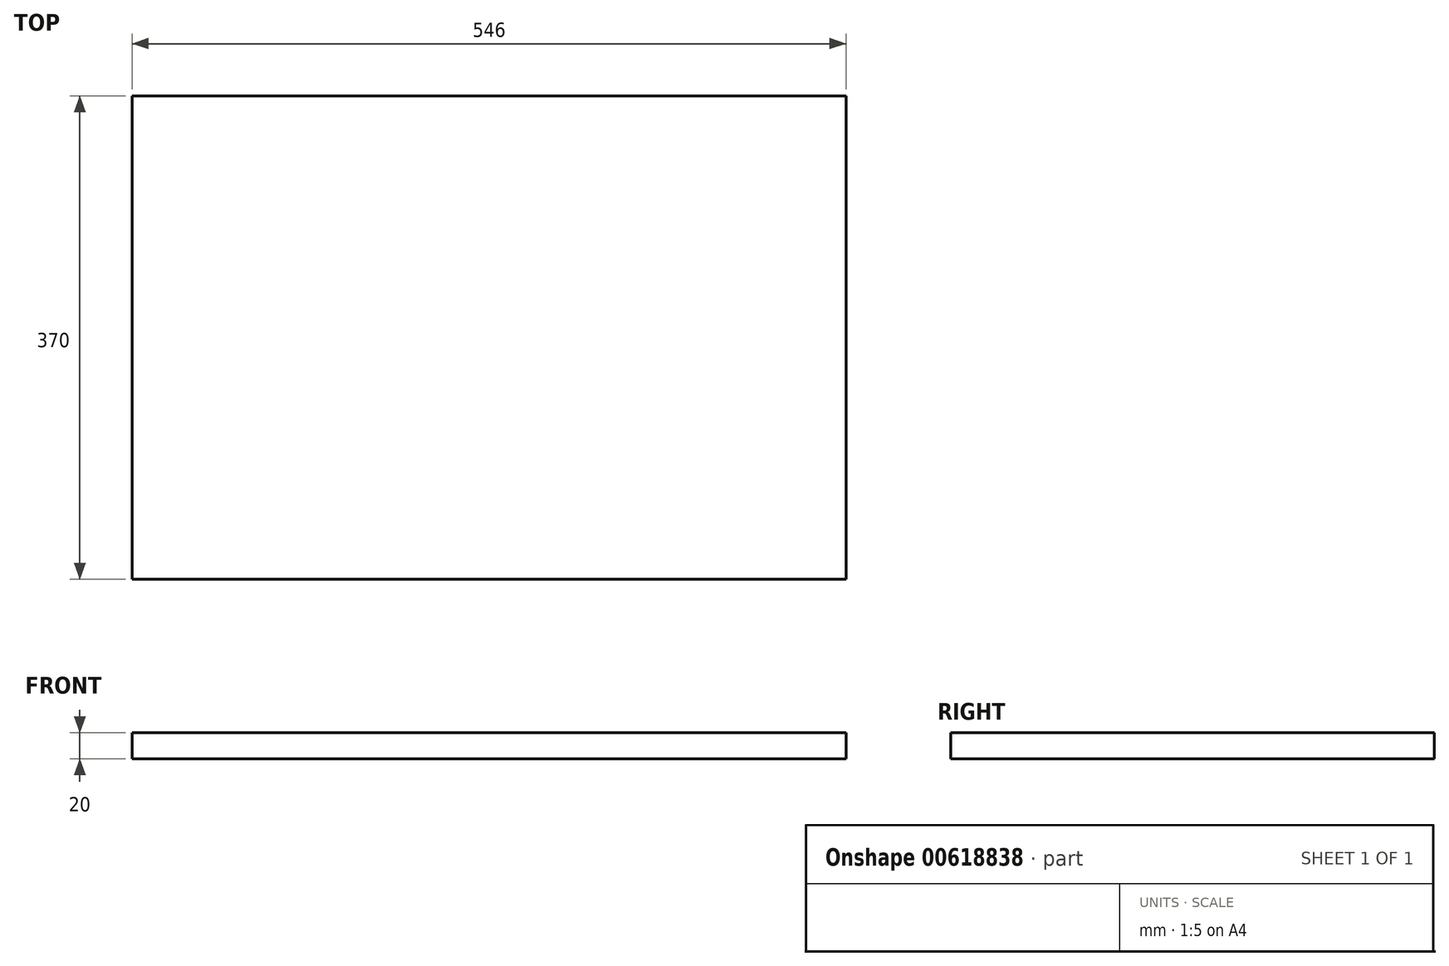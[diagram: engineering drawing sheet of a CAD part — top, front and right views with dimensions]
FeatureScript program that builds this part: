
annotation { "Feature Type Name" : "Feature", "Feature Type Description" : "" }
export const myFeature = defineFeature(function(context is Context, id is Id, definition is map)
    precondition{}
    {
        {
            var Q0;
            Q0=qCreatedBy(makeId("Top.planeOp"),FACE);
            var sketch = newSketch(context, id + "F0", { "sketchPlane" : qUnion([Q0])});
            skLineSegment(sketch, "E0.bottom", {"start": v(-273, 185) * mm, "end": v(273, 185) * mm});
            skLineSegment(sketch, "E0.top", {"start": v(-273, -185) * mm, "end": v(273, -185) * mm});
            skLineSegment(sketch, "E0.left", {"start": v(-273, 185) * mm, "end": v(-273, -185) * mm});
            skLineSegment(sketch, "E0.right", {"start": v(273, 185) * mm, "end": v(273, -185) * mm});
            skPoint(sketch, "E0.middle", {"position": v(0, 0) * mm});
            skSolve(sketch);
        }
        {
            var Q0;
            Q0 = qSketchRegion(id + "F0", true);
            extrude(context, id + "F1", {"entities" : qUnion([Q0]), "depth" : 20 * mm, "offsetDistance" : 25 * mm});
        }
    });
